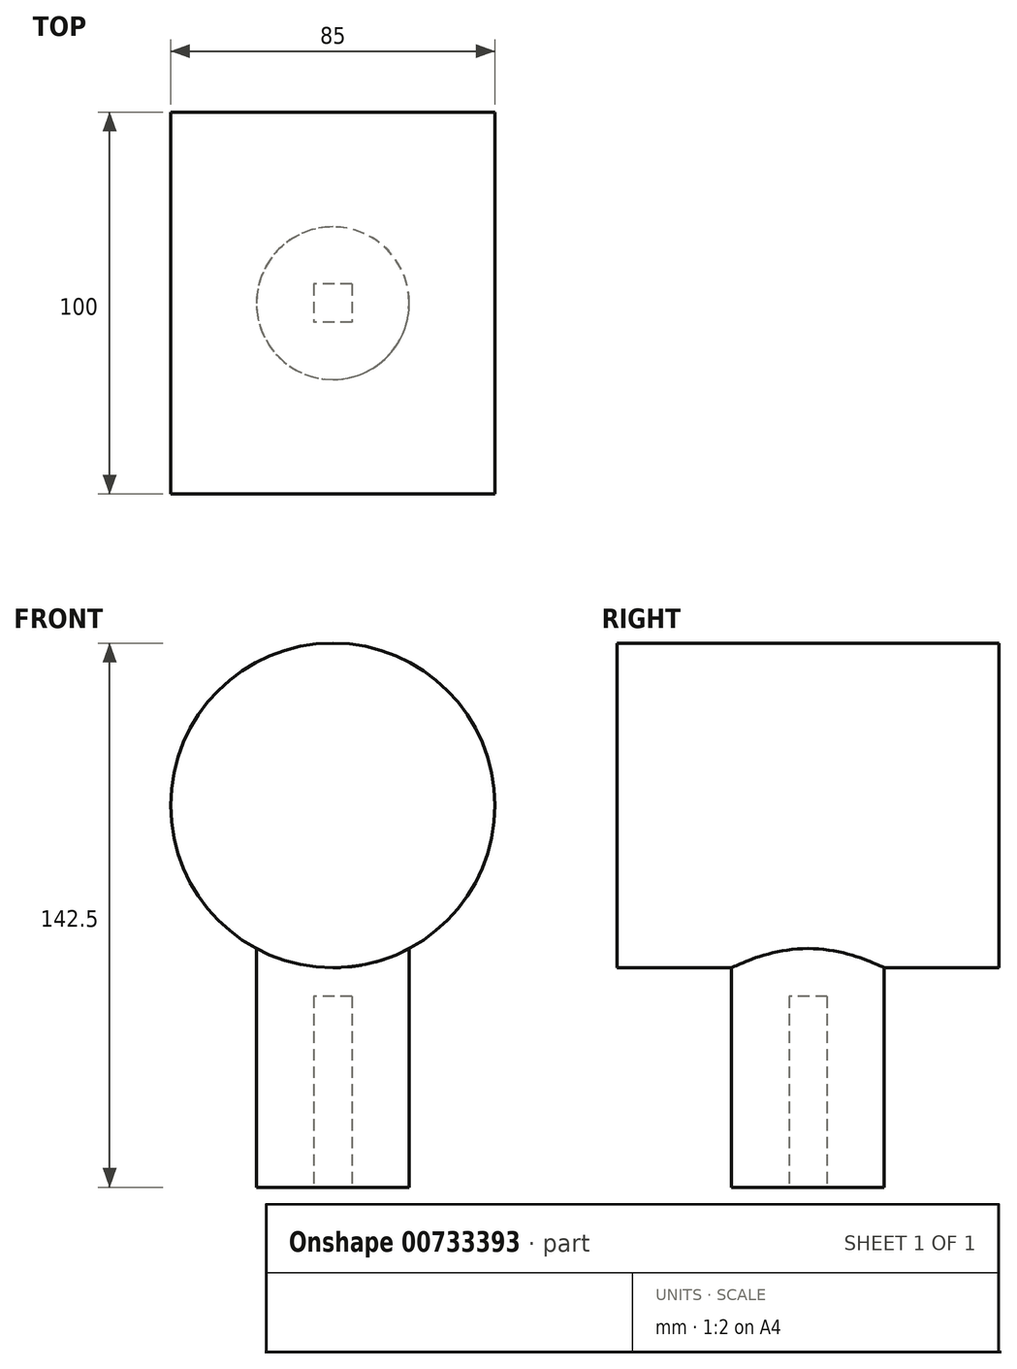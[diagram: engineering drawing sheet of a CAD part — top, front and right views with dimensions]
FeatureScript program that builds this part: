
annotation { "Feature Type Name" : "Feature", "Feature Type Description" : "" }
export const myFeature = defineFeature(function(context is Context, id is Id, definition is map)
    precondition{}
    {
        {
            var Q0;
            Q0=qCreatedBy(makeId("Front.planeOp"),FACE);
            var sketch = newSketch(context, id + "F0", { "sketchPlane" : qUnion([Q0])});
            skCircle(sketch, "E0", {"center": v(0, 0) * mm, "radius": 42.5 * mm});
            skSolve(sketch);
        }
        {
            var Q0;
            Q0 = qSketchRegion(id + "F0", true);
            extrude(context, id + "F1", {"entities" : qUnion([Q0]), "endBound" : BoundingType.SYMMETRIC, "depth" : 100 * mm, "offsetDistance" : 25 * mm});
        }
        {
            var Q0;
            Q0=qCreatedBy(makeId("Top.planeOp"),FACE);
            var sketch = newSketch(context, id + "F2", { "sketchPlane" : qUnion([Q0])});
            skCircle(sketch, "E1", {"center": v(0, 0) * mm, "radius": 20 * mm});
            skSolve(sketch);
        }
        {
            var Q0;
            Q0 = qSketchRegion(id + "F2", true);
            extrude(context, id + "F3", {"entities" : qUnion([Q0]), "operationType" : NewBodyOperationType.ADD, "oppositeDirection" : true, "depth" : 100 * mm, "offsetDistance" : 25 * mm});
        }
        {
            var Q0;
            Q0=makeQuery(id+"F3.opExtrude","CAP_FACE",FACE,{"disambiguationData":[OSD([sQuery(id+"F2.wireOp",EDGE,"E1")])],"isStart":false});
            var sketch = newSketch(context, id + "F4", { "sketchPlane" : qUnion([Q0])});
            skLineSegment(sketch, "E2.bottom", {"start": v(5, -5) * mm, "end": v(-5, -5) * mm});
            skLineSegment(sketch, "E2.top", {"start": v(5, 5) * mm, "end": v(-5, 5) * mm});
            skLineSegment(sketch, "E2.left", {"start": v(5, -5) * mm, "end": v(5, 5) * mm});
            skLineSegment(sketch, "E2.right", {"start": v(-5, -5) * mm, "end": v(-5, 5) * mm});
            skPoint(sketch, "E2.middle", {"position": v(0, 0) * mm});
            skSolve(sketch);
        }
        {
            var Q0;
            Q0=makeQuery(id+"F4.imprint","IMPRINT",FACE,{"disambiguationData":[TD([[makeQuery(id+"F4.imprint","IMPRINT",EDGE,{"derivedFrom":sQuery(id+"F4.wireOp",EDGE,"E2.bottom")}),-1.0]])]});
            extrude(context, id + "F5", {"entities" : qUnion([Q0]), "operationType" : NewBodyOperationType.REMOVE, "oppositeDirection" : true, "depth" : 50 * mm, "offsetDistance" : 25 * mm});
        }
    });
